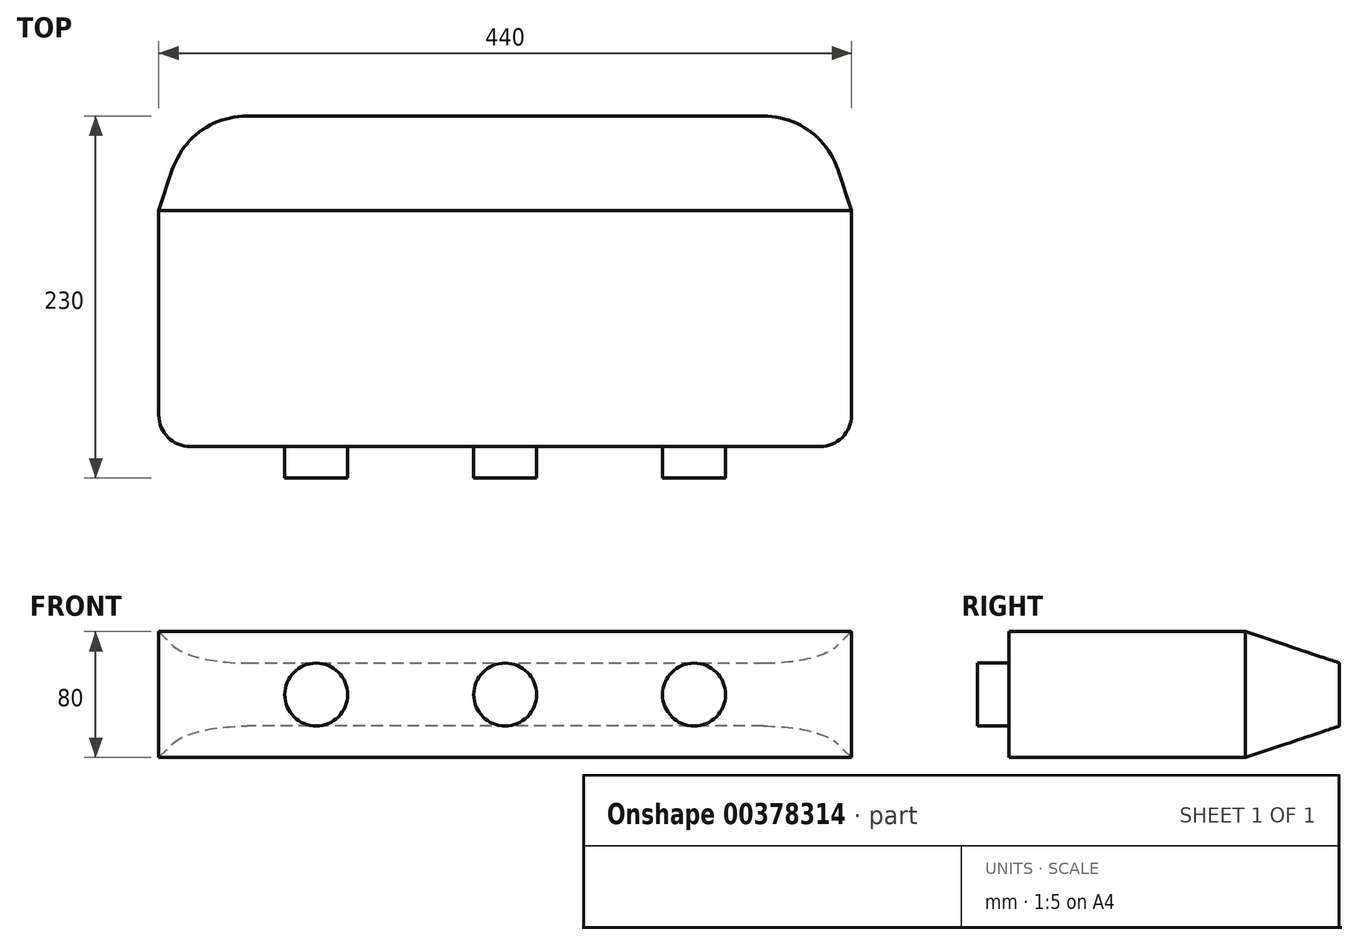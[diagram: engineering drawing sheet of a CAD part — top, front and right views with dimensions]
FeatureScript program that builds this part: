
annotation { "Feature Type Name" : "Feature", "Feature Type Description" : "" }
export const myFeature = defineFeature(function(context is Context, id is Id, definition is map)
    precondition{}
    {
        {
            var Q0;
            Q0=qCreatedBy(makeId("Top.planeOp"),FACE);
            var sketch = newSketch(context, id + "F0", { "sketchPlane" : qUnion([Q0])});
            skLineSegment(sketch, "E0.bottom", {"start": v(0, 0) * mm, "end": v(440, 0) * mm});
            skLineSegment(sketch, "E0.top", {"start": v(0, 210) * mm, "end": v(440, 210) * mm});
            skLineSegment(sketch, "E0.left", {"start": v(0, 0) * mm, "end": v(0, 210) * mm});
            skLineSegment(sketch, "E0.right", {"start": v(440, 0) * mm, "end": v(440, 210) * mm});
            skSolve(sketch);
        }
        {
            var Q0;
            Q0 = qSketchRegion(id + "F0", true);
            extrude(context, id + "F1", {"entities" : qUnion([Q0]), "depth" : 80 * mm});
        }
        {
            var Q0;
            Q0=makeQuery(id+"F1.opExtrude","SWEPT_FACE",FACE,{"disambiguationData":[OSD([sQuery(id+"F0.wireOp",EDGE,"E0.top")])]});
            chamfer(context, id + "F2", {"entities" : qUnion([Q0]), "chamferType" : ChamferType.TWO_OFFSETS, "width1" : 60 * mm, "oppositeDirection" : false, "width2" : 20 * mm, "tangentPropagation" : true});
        }
        {
            var Q0;
            {var subQ0=sQuery(id+"F0.wireOp",EDGE,"E0.top");Q0=makeQuery(id+"F2.opChamfer","BLEND_EDGE",EDGE,{"blendedFrom":[makeQuery(id+"F1.opExtrude","SWEPT_EDGE",EDGE,{"disambiguationData":[OSD([subQ0,sQuery(id+"F0.wireOp",EDGE,"E0.left")])]}),makeQuery(id+"F1.opExtrude","SWEPT_FACE",FACE,{"disambiguationData":[OSD([subQ0])]})],"blendedInto":[makeQuery(id+"F1.opExtrude","SWEPT_FACE",FACE,{"disambiguationData":[OSD([subQ0])]})]});}
            fillet(context, id + "F3", {"entities" : qUnion([Q0]), "radius" : 50 * mm, "tangentPropagation" : true, "allowEdgeOverflow" : false});
        }
        {
            var Q0;
            {var subQ0=sQuery(id+"F0.wireOp",EDGE,"E0.top");Q0=makeQuery(id+"F2.opChamfer","BLEND_EDGE",EDGE,{"blendedFrom":[makeQuery(id+"F1.opExtrude","SWEPT_EDGE",EDGE,{"disambiguationData":[OSD([subQ0,sQuery(id+"F0.wireOp",EDGE,"E0.right")])]}),makeQuery(id+"F1.opExtrude","SWEPT_FACE",FACE,{"disambiguationData":[OSD([subQ0])]})],"blendedInto":[makeQuery(id+"F1.opExtrude","SWEPT_FACE",FACE,{"disambiguationData":[OSD([subQ0])]})]});}
            fillet(context, id + "F4", {"entities" : qUnion([Q0]), "radius" : 50 * mm, "tangentPropagation" : true, "allowEdgeOverflow" : false});
        }
        {
            var Q0;
            Q0=makeQuery(id+"F1.opExtrude","SWEPT_EDGE",EDGE,{"disambiguationData":[OSD([sQuery(id+"F0.wireOp",EDGE,"E0.bottom"),sQuery(id+"F0.wireOp",EDGE,"E0.left")])]});
            fillet(context, id + "F5", {"entities" : qUnion([Q0]), "radius" : 20 * mm, "tangentPropagation" : true, "allowEdgeOverflow" : false});
        }
        {
            var Q0;
            Q0=makeQuery(id+"F1.opExtrude","SWEPT_EDGE",EDGE,{"disambiguationData":[OSD([sQuery(id+"F0.wireOp",EDGE,"E0.bottom"),sQuery(id+"F0.wireOp",EDGE,"E0.right")])]});
            fillet(context, id + "F6", {"entities" : qUnion([Q0]), "radius" : 20 * mm, "tangentPropagation" : true, "allowEdgeOverflow" : false});
        }
        {
            var Q0;
            Q0=makeQuery(id+"F1.opExtrude","SWEPT_FACE",FACE,{"disambiguationData":[OSD([sQuery(id+"F0.wireOp",EDGE,"E0.bottom")])]});
            var sketch = newSketch(context, id + "F7", { "sketchPlane" : qUnion([Q0])});
            skCircle(sketch, "E1", {"center": v(100, 40) * mm, "radius": 20 * mm});
            skCircle(sketch, "E2.1.0.0", {"center": v(220, 40) * mm, "radius": 20 * mm});
            skCircle(sketch, "E2.2.0.0", {"center": v(340, 40) * mm, "radius": 20 * mm});
            skLineSegment(sketch, "E2.direction1", {"start": v(50, 40) * mm, "end": v(170, 40) * mm, "construction": true});
            skSolve(sketch);
        }
        {
            var Q0;
            Q0 = qSketchRegion(id + "F7", true);
            extrude(context, id + "F8", {"entities" : qUnion([Q0]), "operationType" : NewBodyOperationType.ADD, "depth" : 20 * mm});
        }
    });
